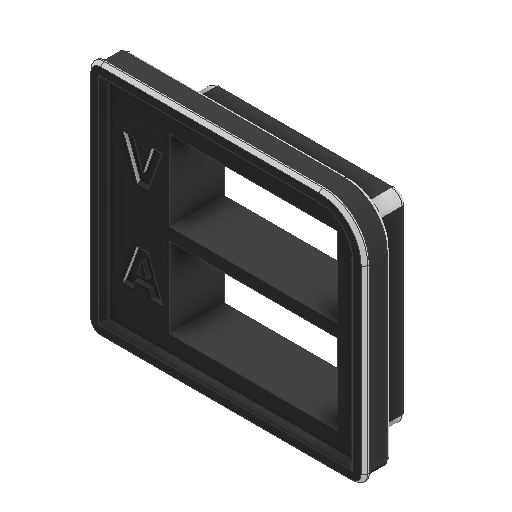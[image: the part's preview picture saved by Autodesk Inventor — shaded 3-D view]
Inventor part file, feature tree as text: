
AUTODESK INVENTOR PART (.ipt)
format: ipt  version: 2025 (Build 290162000, 162)  size: 365,056 bytes
history: native  units: mm
features: reference x51, sketch x9, extrude x6, other x6, fillet x2, emboss x1, sweep x1, projected_geometry x1
ambient origin geometry x8: Origin, YZ Plane, XZ Plane, XY Plane, X Axis, Y Axis, Z Axis, Center Point
bodies: Solid1 (feature_tree)
feature tree (77):
  extrude  "Extrusion1"  Depth=50.0mm
  extrude  "Extrusion2"  Depth=7.0mm TaperAngle=0.0deg
  extrude  "Extrusion3"  Depth=1.1mm
  extrude  "Extrusion4"  Depth=0.35mm
  extrude  "Extrusion5"  Depth=4.0mm TaperAngle=0.0deg
  extrude  "Extrusion6"  Depth=15.0mm
  emboss  "Emboss1"
  fillet  "Fillet3"  Radius=8.726646mm
  fillet  "Fillet2"  Radius=6.981317mm
  sweep  "Sweep3"
  sketch  "Sketch1"  dims[d0=60.0mm d1=50.0mm]
  sketch  "Sketch2"  dims[d2=7.0mm d3=0.0mm d6=7.0mm d7=0.0mm]
  sketch  "Sketch3"  dims[d8=1.1mm d9=0.0mm d10=3.0mm]
  reference  "Reference2"
  sketch  "Sketch4"  dims[d11=4.0mm d12=0.0mm d13=0.35mm]
  reference  "Reference3"
  reference  "Reference4"
  reference  "Reference5"
  reference  "Reference6"
  reference  "Reference7"
  reference  "Reference8"
  reference  "Reference9"
  reference  "Reference10"
  sketch  "Sketch5"  dims[d14=0.35mm d15=4.0mm d16=0.0mm]
  reference  "Reference11"
  reference  "Reference12"
  reference  "Reference13"
  reference  "Reference14"
  reference  "Reference15"
  reference  "Reference16"
  reference  "Reference17"
  reference  "Reference18"
  reference  "Reference21"
  reference  "Reference22"
  reference  "Reference23"
  reference  "Reference24"
  reference  "Reference25"
  reference  "Reference26"
  reference  "Reference27"
  reference  "Reference28"
  reference  "Reference29"
  reference  "Reference30"
  reference  "Reference31"
  reference  "Reference32"
  reference  "Reference33"
  reference  "Reference34"
  reference  "Reference35"
  reference  "Reference36"
  sketch  "Sketch11"  dims[d27=0.25mm d29=15.0mm d38=8.726646mm d39=6.981317mm]
  reference  "Reference37"
  sketch  "Sketch12"  dims[d40=0.3mm d43=0.75mm]
  reference  "Reference39"
  sketch  "Sketch13"  dims[d46=3.5mm d48=0.7mm d49=0.0mm d52=8.0mm d53=16.0mm d54=8.0mm d55=8.0mm d56=1.5mm d57=0.0mm d58=2.0mm d59=0.0mm d60=0.0mm d62=7.39429mm d64=1.4mm d65=7.3mm d66=3.5mm d67=7.026096mm d68=1.4mm]
  reference  "Reference40"
  reference  "Reference41"
  projected_geometry  "Projected Loop3"
  reference  "Reference42"
  reference  "Reference43"
  reference  "Reference44"
  reference  "Reference45"
  reference  "Reference46"
  reference  "Reference47"
  reference  "Reference48"
  reference  "Reference49"
  reference  "Reference50"
  reference  "Reference51"
  reference  "Reference52"
  reference  "Reference53"
  reference  "Reference54"
  reference  "Reference55"
  sketch  "3D Sketch3"
  other  "USB_C_PD_PPS_sink_with_enclosure.iam"
  other  "top_enclosure:1"
  other  "USB_C_PD_PPS_sink:1"
  other  "3461AS_3461AS-1:2"
  other  "3461AS_3461AS-1:1"
  other  "G800LW304032EU-Footprint-1_CMP-002-00028-3:1"
